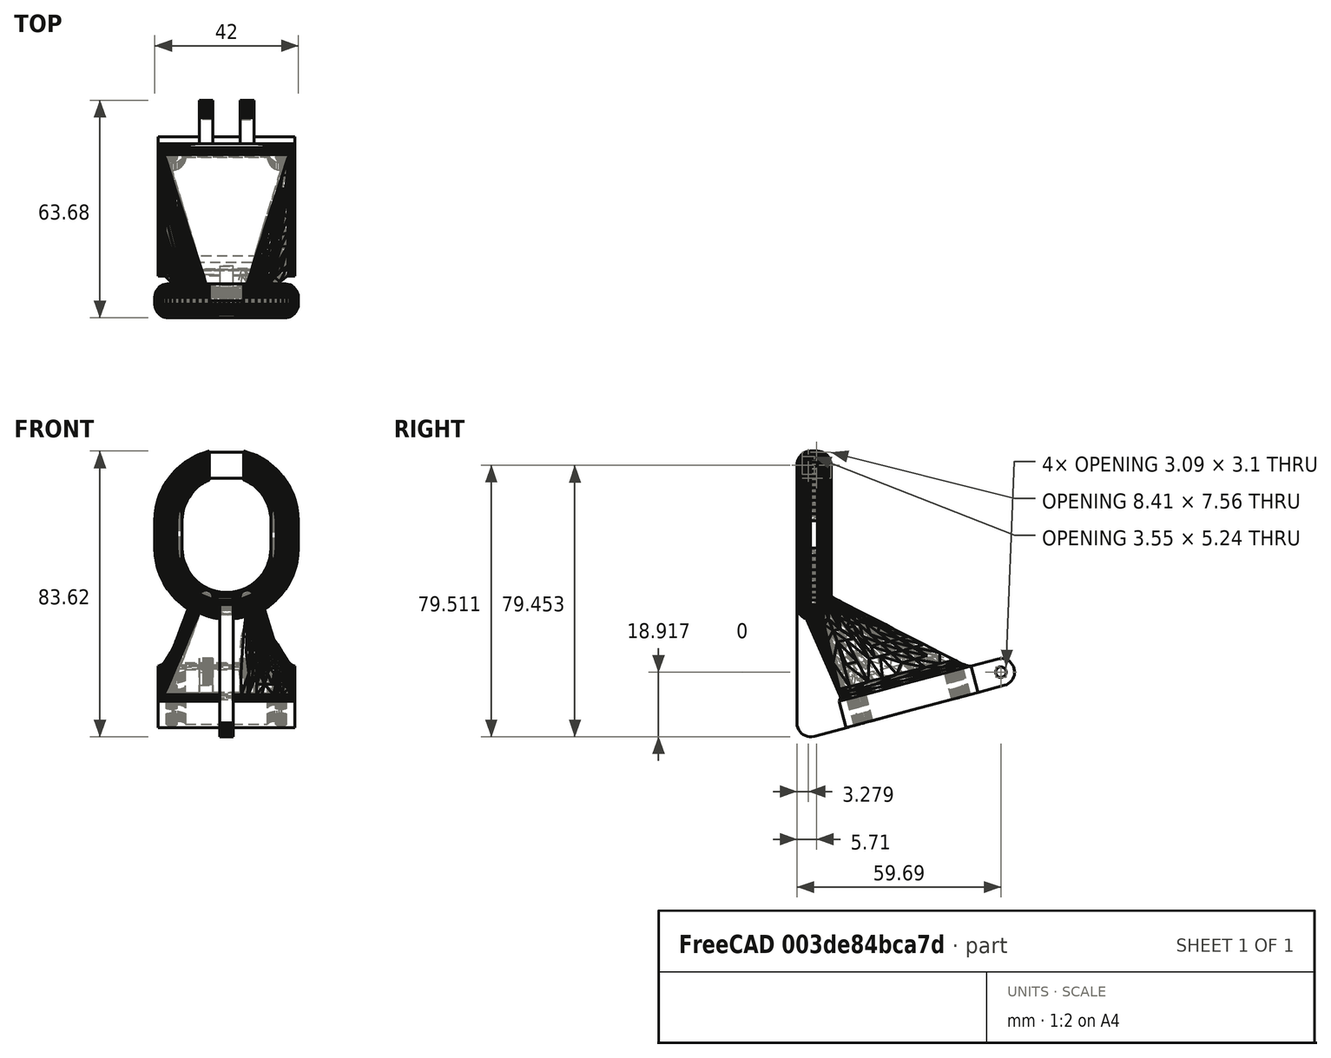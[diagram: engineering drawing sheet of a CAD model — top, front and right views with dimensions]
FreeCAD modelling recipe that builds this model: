
FCSTD DOCUMENT  (FreeCAD 0.16R6703 (Git))
Label: COrrecao
License: FreeArt
LicenseURL: http://artlibre.org/licence/lal
objects: Part::Feature×1, Sketcher::SketchObject×1, PartDesign::Pad×1
note: 4 computed .brp shape members not serialized (recipe doc carries the construction recipe); baked Part::Feature solids carry a one-line shape summary decoded from their .brp

FEATURE [Part::Feature] Solid
  shape: bbox 42 x 63.69 x 83.62 mm, 14206 faces (baked)
FEATURE [Sketcher::SketchObject] Sketch
  Placement = pos=(16,0,0) rot=(0.57735,0.57735,0.57735;2.0944rad)
  Support = -> Solid [Face14009]
  sketch-geometry (4):
    g0: ArcOfCircle CenterX=6.92213 CenterY=79.485 CenterZ=0 NormalX=0 NormalY=0 NormalZ=1 Radius=3.74484 StartAngle=4.73674 EndAngle=7.79746
    g1: LineSegment StartX=7.13366 StartY=83.2239 StartZ=0 EndX=5.76907 EndY=83.3011 EndZ=0
    g2: LineSegment StartX=5.76907 StartY=83.3011 StartZ=0 EndX=5.76907 EndY=75.7413 EndZ=0
    g3: LineSegment StartX=5.76907 StartY=75.7413 StartZ=0 EndX=7.0133 EndY=75.7413 EndZ=0
  constraints (8):
    c: Tangent(g0,g1) = -1.5708
    c: Coincident(g1,g2)
    c: Vertical(g2)
    c: Coincident(g2,g3)
    c: Coincident(g3,g0)
    c: Horizontal(g3)
    c: DistanceX(g-2,g0) = 6.92213
    c: DistanceX(g-2,g2) = 5.76907
FEATURE [PartDesign::Pad] Pad
  Length = 10
  Length2 = 100
  Sketch = -> Sketch
  Type = 0
